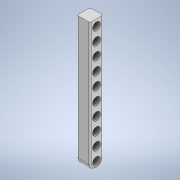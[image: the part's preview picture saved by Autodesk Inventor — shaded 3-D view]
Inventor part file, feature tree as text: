
AUTODESK INVENTOR PART (.ipt)
format: ipt  version: 2022 (Build 260153000, 153)  size: 152,576 bytes
history: native  units: mm
features: extrude x2, sketch x2, fillet x1, projected_geometry x1
ambient origin geometry x8: Origin, YZ Plane, XZ Plane, XY Plane, X Axis, Y Axis, Z Axis, Center Point
bodies: Solid1 (feature_tree)
feature tree (6):
  extrude  "Extrusion1"  Depth=10.0mm
  extrude  "Extrusion2"  Depth=1.0mm
  fillet  "Fillet1"  Radius=5.0mm
  sketch  "Sketch1"  dims[d0=10.0mm d1=10.0mm]
  sketch  "Sketch2"  dims[d2=100.0mm d3=0.0mm d4=6.0mm d5=5.0mm d6=5.0mm d7=100.0mm d9=10.0mm d10=10.0mm d12=10.0mm d14=0.0mm d15=0.0mm d16=1.0mm]
  projected_geometry  "Projected Loop1"
